# Revit family: UNIVERSAL
name_source: partatom
category: Осветительные приборы
units: mm (PartAtom-declared; Revit-internal decimal feet)

## family parameters
Всегда вертикально = Нет
Источник света = Да
На основе рабочей плоскости = Нет
Общий = Нет
При загрузке вырезать с полостями = Нет
Размер круглого соединителя = Использовать диаметр
Тип детали = Нормальный
Точка расчета площади = Да

## types (12) — shared parameters
ADSK_Единица измерения = шт.
ADSK_Завод-изготовитель = ЗАО «Центрстройсвет»
ADSK_Классификация нагрузок = Прочее
ADSK_Количество фаз = 1
ADSK_Количество фаз числовое = 1
ADSK_Коэффициент мощности = 0.92
ADSK_Масса = 3
ADSK_Напряжение = 230 В
ADSK_Ток = 0 А
URL = http://csvt.ru
Видимая форма излучения при визуализации = Да
Высота = 55 мм
Изготовитель = ЗАО «Центрстройсвет»
Материал светильника = RAL 9001
Материал стекла = RAL светящийся
Светофильтр = 16777215
Смещение цветовой температуры при затухании лампы = <Нет>
Угол наклона = 90.00°

## per-type parameters (varying)
| type | ADSK_Код изделия | ADSK_Наименование | ADSK_Номинальная мощность | ADSK_Обозначение | ADSK_Полная мощность | Длина | Излучение по длине прямоугольника | Излучение по ширине прямоугольника | Файл фотометрической сетки | Ширина |
| CSVT Universal - 34/opal-sand 595x595х55 (IP20, 4000К) | ЦБ000007790 | Универсальный светодиодный светильник CSVT Universal - 34/opal-sand 595x595х55 (IP20, 4000К) | 32 Вт | CSVT Universal - 34/opal-sand 595x595х55 (IP20, 4000К) | 35 В·А | 595 мм | 555 мм | 555 мм | CSVT Universal-34_opal-sand.ies | 595 мм |
| CSVT Universal - 34/opal- sand 595x595х55 (IP20, 4000К) с БАП на 1 час | ЦБ000007797 | Универсальный светодиодный светильник CSVT Universal - 34/opal- sand 595x595х55 (IP20, 4000К) с БАП на 1 час | 32 Вт | CSVT Universal - 34/opal- sand 595x595х55 (IP20, 4000К) | 35 В·А | 595 мм | 555 мм | 555 мм | CSVT Universal-34_opal-sand.ies | 595 мм |
| CSVT Universal - 34/opa-sand 595x595х55 (IP20, 4000К) с БАП на 3 часа | ЦБ000007798 | Универсальный светодиодный светильник CSVT Universal - 34/opa-sand 595x595х55 (IP20, 4000К) с БАП на 3 часа | 32 Вт | CSVT Universal - 34/opal- sand 595x595х55 (IP20, 4000К) | 35 В·А | 595 мм | 555 мм | 555 мм | CSVT Universal-34_opal-sand.ies | 595 мм |
| CSVT Universal - 34/prisma 595х595х55 (IP20, 4000К) | ЦБ000005855 | Универсальный светодиодный светильник CSVT Universal - 34/prisma 595х595х55 (IP20, 4000К) | 32 Вт | CSVT Universal - 34/prisma 595х595х55 (IP20, 4000К) | 35 В·А | 595 мм | 555 мм | 555 мм | CSVT Universal-34_opal-sand.ies | 595 мм |
| CSVT Universal - 34/prisma 595х595х55 (IP20, 4000К) с БАП на 1 час | ЦБ000007895 | Универсальный светодиодный светильник CSVT Universal - 34/prisma 595х595х55 (IP20, 4000К) с БАП на 1 час | 32 Вт | CSVT Universal - 34/prisma 595х595х55 (IP20, 4000К) | 35 В·А | 595 мм | 555 мм | 555 мм | CSVT Universal-34_opal-sand.ies | 595 мм |
| CSVT Universal - 34/prisma 595х595х55(IP20, 4000К) с БАП на 3 часа | ЦБ000007896 | Универсальный светодиодный светильник CSVT Universal - 34/prisma 595х595х55(IP20, 4000К) с БАП на 3 часа | 32 Вт | CSVT Universal - 34/prisma 595х595х55 (IP20, 4000К) | 35 В·А | 595 мм | 555 мм | 555 мм | CSVT Universal-34_opal-sand.ies | 595 мм |
| CSVT Universal - 50/opal-sand 595x595х55 (IP20, 4000К) | ЦБ000007791 | Универсальный светодиодный светильник CSVT Universal - 50/opal-sand 595x595х55 (IP20, 4000К) | 48 Вт | CSVT Universal - 50/opal-sand 595x595х55 (IP20, 4000К) | 52 В·А | 595 мм | 555 мм | 555 мм | CSVT Universal-50_opal-sand.ies | 595 мм |
| CSVT Universal - 50/prisma 595x595х55 (IP20, 4000К) | ЦБ000007897 | Универсальный светодиодный светильник CSVT Universal - 50/prisma 595x595х55 (IP20, 4000К) | 48 Вт | CSVT Universal - 50/prisma 595x595х55 (IP20, 4000К) | 52 В·А | 595 мм | 555 мм | 555 мм | Светильник UNIVERSAL-50 PRISMA-(595х595).IES | 595 мм |
| CSVT Universal - 38/opal-sand 295х1195х55 (IP20, 4000К) | ЦБ000007907 | Универсальный светодиодный светильник CSVT Universal - 38/opal-sand 295х1195х55 (IP20, 4000К) | 38 Вт | CSVT Universal - 38/opal-sand 295х1195х55 (IP20, 4000К) | 41 В·А | 1195 мм | 1155 мм | 255 мм | Светильник UNIVERSAL-38 OPAL-SAND-(295x1195).IES | 295 мм |
| CSVT Universal - 38/opal-sand 295х1195х55 (IP20, 4000К) с БАП на 1 час | ЦБ000007926 | Универсальный светодиодный светильник CSVT Universal - 38/opal-sand 295х1195х55 (IP20, 4000К) с БАП на 1 час | 38 Вт | CSVT Universal - 38/opal-sand 295х1195х55 (IP20, 4000К) | 41 В·А | 1195 мм | 1155 мм | 255 мм | Светильник UNIVERSAL-38 OPAL-SAND-(295x1195).IES | 295 мм |
| CSVT Universal - 38/opal-sand 295х1195х55 (IP20, 4000К) с БАП на 3 часа | ЦБ000007928 | Универсальный светодиодный светильник CSVT Universal - 38/opal-sand 295х1195х55 (IP20, 4000К) с БАП на 3 часа | 38 Вт | CSVT Universal - 38/opal-sand 295х1195х55 (IP20, 4000К) | 41 В·А | 1195 мм | 1155 мм | 255 мм | Светильник UNIVERSAL-38 OPAL-SAND-(295x1195).IES | 295 мм |
| CSVT Universal - 76/opal-sand 295x1195х55 (IP20, 4000К) | ЦБ000007923 | Универсальный светодиодный светильник CSVT Universal - 76/opal-sand 295x1195х55 (IP20, 4000К) | 76 Вт | CSVT Universal - 76/opal-sand 295x1195х55 (IP20, 4000К) | 83 В·А | 1195 мм | 1155 мм | 255 мм | Светильник UNIVERSAL-76 OPAL-SAND-(295x1195).ies | 295 мм |
